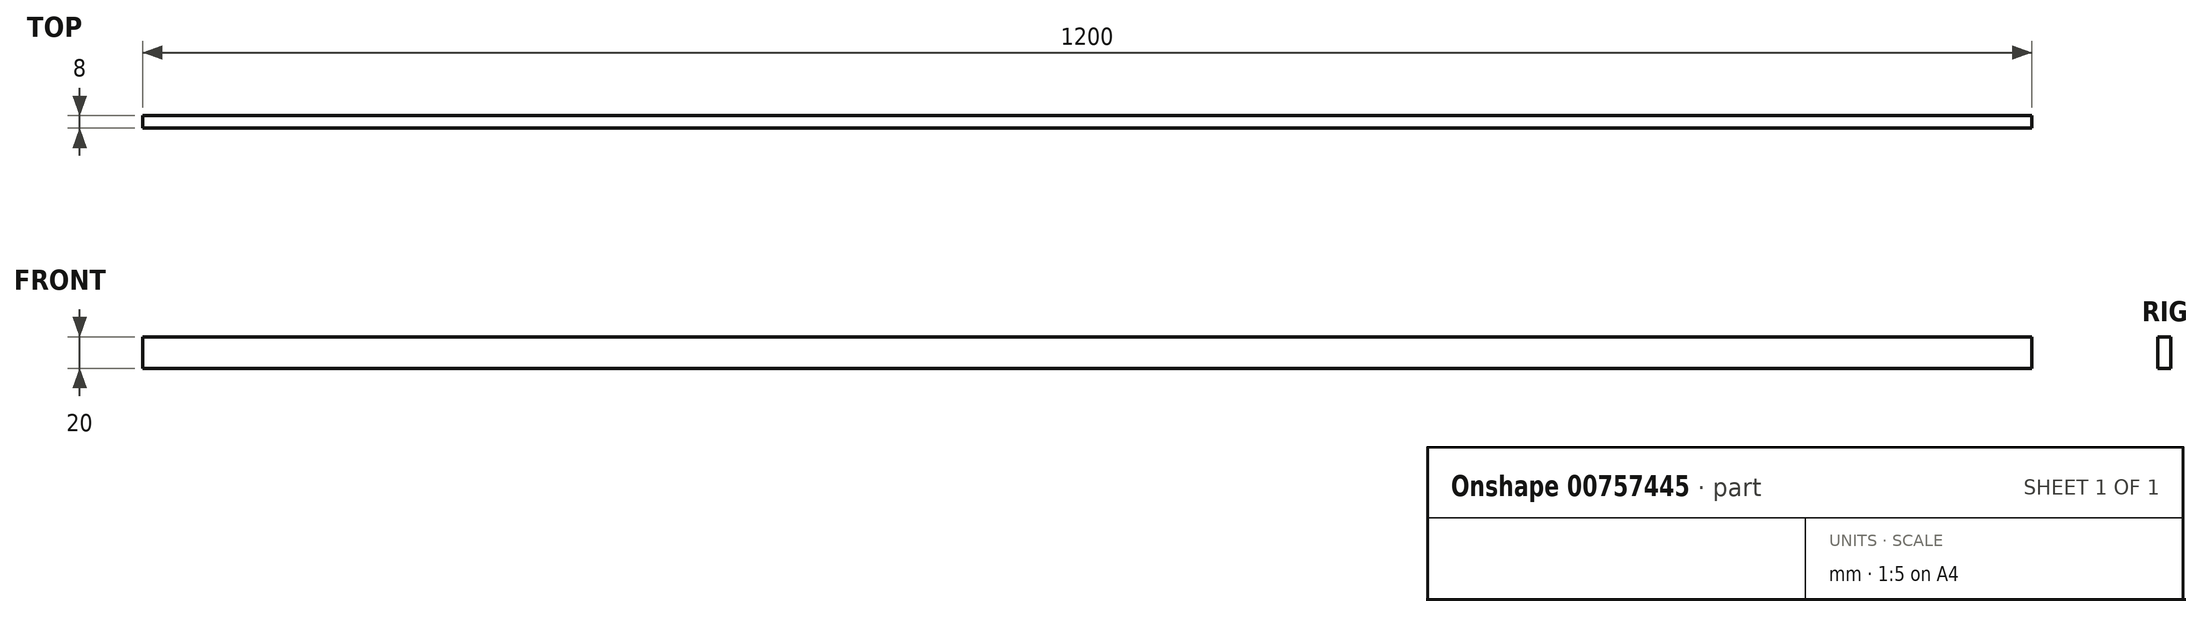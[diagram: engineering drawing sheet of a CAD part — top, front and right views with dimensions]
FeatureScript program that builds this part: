
annotation { "Feature Type Name" : "Feature", "Feature Type Description" : "" }
export const myFeature = defineFeature(function(context is Context, id is Id, definition is map)
    precondition{}
    {
        {
            var Q0;
            Q0=qCreatedBy(makeId("Right.planeOp"),FACE);
            var sketch = newSketch(context, id + "F0", { "sketchPlane" : qUnion([Q0])});
            skLineSegment(sketch, "E0.bottom", {"start": v(-4, 10) * mm, "end": v(4, 10) * mm});
            skLineSegment(sketch, "E0.top", {"start": v(-4, -10) * mm, "end": v(4, -10) * mm});
            skLineSegment(sketch, "E0.left", {"start": v(-4, 10) * mm, "end": v(-4, -10) * mm});
            skLineSegment(sketch, "E0.right", {"start": v(4, 10) * mm, "end": v(4, -10) * mm});
            skSolve(sketch);
        }
        {
            var Q0;
            Q0=makeQuery(id+"F0.imprint","IMPRINT",FACE,{"disambiguationData":[TD([[makeQuery(id+"F0.imprint","IMPRINT",EDGE,{"derivedFrom":sQuery(id+"F0.wireOp",EDGE,"E0.bottom")}),-1.0]])]});
            extrude(context, id + "F1", {"entities" : qUnion([Q0]), "endBound" : BoundingType.SYMMETRIC, "depth" : 1200 * mm, "offsetDistance" : 25 * mm});
        }
    });
